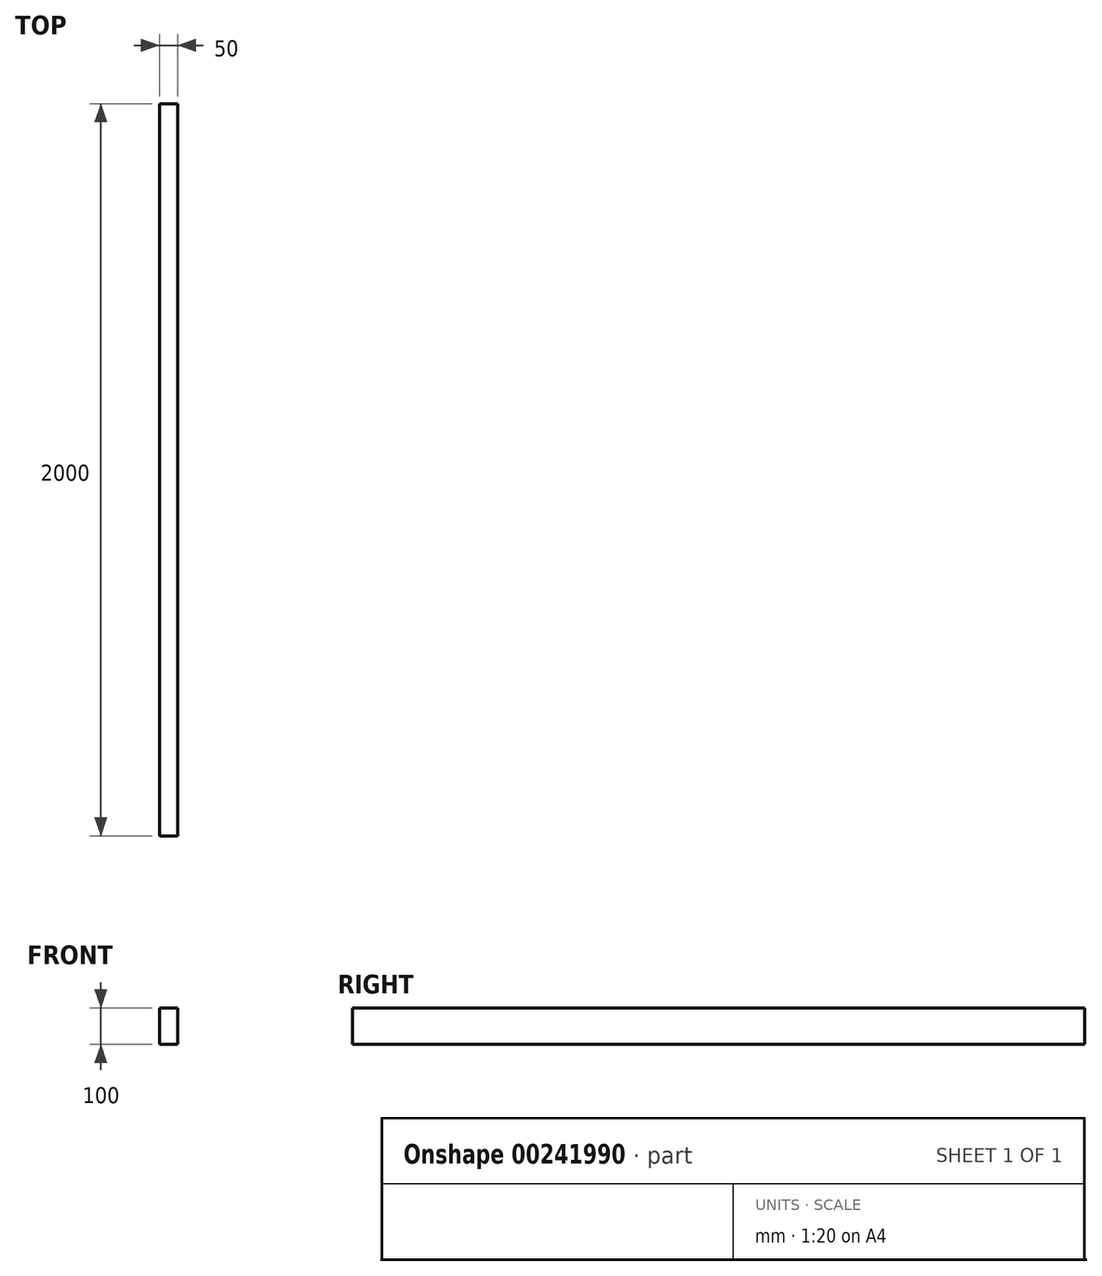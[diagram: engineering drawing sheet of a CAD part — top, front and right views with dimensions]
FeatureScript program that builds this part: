
annotation { "Feature Type Name" : "Feature", "Feature Type Description" : "" }
export const myFeature = defineFeature(function(context is Context, id is Id, definition is map)
    precondition{}
    {
        {
            var Q0;
            Q0=qCreatedBy(makeId("Front.planeOp"),FACE);
            var sketch = newSketch(context, id + "F0", { "sketchPlane" : qUnion([Q0])});
            skLineSegment(sketch, "E0.bottom", {"start": v(25, 50) * mm, "end": v(-25, 50) * mm});
            skLineSegment(sketch, "E0.top", {"start": v(25, -50) * mm, "end": v(-25, -50) * mm});
            skLineSegment(sketch, "E0.left", {"start": v(25, 50) * mm, "end": v(25, -50) * mm});
            skLineSegment(sketch, "E0.right", {"start": v(-25, 50) * mm, "end": v(-25, -50) * mm});
            skPoint(sketch, "E0.middle", {"position": v(0, 0) * mm});
            skSolve(sketch);
        }
        {
            var Q0;
            Q0 = qSketchRegion(id + "F0", true);
            extrude(context, id + "F1", {"entities" : qUnion([Q0]), "depth" : 2000 * mm});
        }
    });
